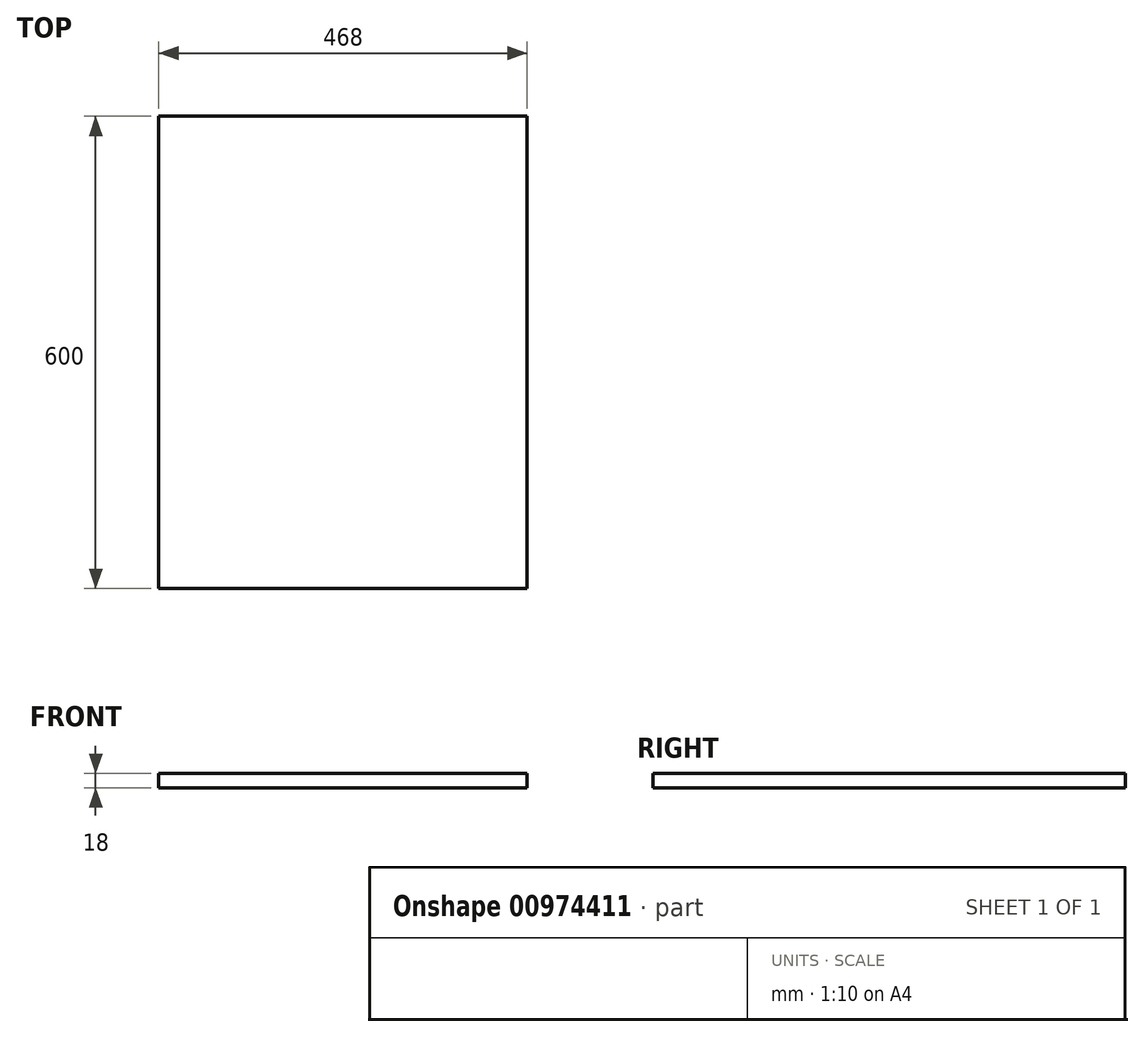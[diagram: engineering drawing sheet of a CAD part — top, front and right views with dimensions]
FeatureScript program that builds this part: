
annotation { "Feature Type Name" : "Feature", "Feature Type Description" : "" }
export const myFeature = defineFeature(function(context is Context, id is Id, definition is map)
    precondition{}
    {
        {
            var Q0;
            Q0=qCreatedBy(makeId("Top.planeOp"),FACE);
            var sketch = newSketch(context, id + "F0", { "sketchPlane" : qUnion([Q0])});
            skLineSegment(sketch, "E0.bottom", {"start": v(234, 300) * mm, "end": v(-234, 300) * mm});
            skLineSegment(sketch, "E0.top", {"start": v(234, -300) * mm, "end": v(-234, -300) * mm});
            skLineSegment(sketch, "E0.left", {"start": v(234, 300) * mm, "end": v(234, -300) * mm});
            skLineSegment(sketch, "E0.right", {"start": v(-234, 300) * mm, "end": v(-234, -300) * mm});
            skPoint(sketch, "E0.middle", {"position": v(0, 0) * mm});
            skSolve(sketch);
        }
        {
            var Q0;
            Q0=makeQuery(id+"F0.imprint","IMPRINT",FACE,{"disambiguationData":[TD([[makeQuery(id+"F0.imprint","IMPRINT",EDGE,{"derivedFrom":sQuery(id+"F0.wireOp",EDGE,"E0.bottom")}),1.0]])]});
            extrude(context, id + "F1", {"entities" : qUnion([Q0]), "depth" : 18 * mm, "offsetDistance" : 25 * mm});
        }
    });
